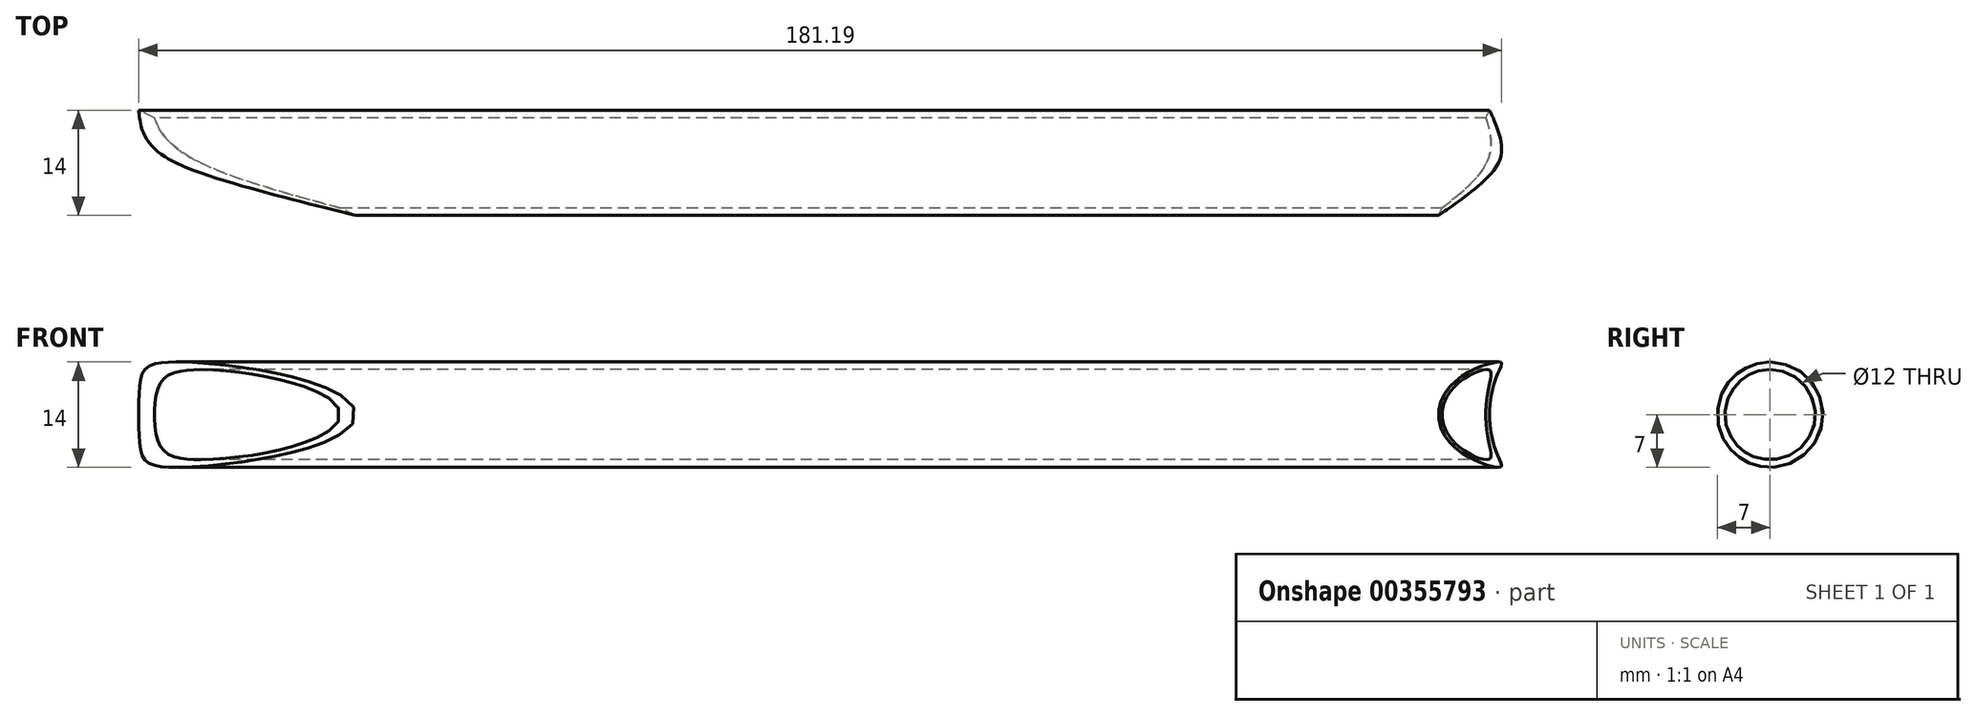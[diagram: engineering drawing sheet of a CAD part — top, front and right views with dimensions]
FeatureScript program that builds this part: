
annotation { "Feature Type Name" : "Feature", "Feature Type Description" : "" }
export const myFeature = defineFeature(function(context is Context, id is Id, definition is map)
    precondition{}
    {
        {
            var Q0;
            Q0=qCreatedBy(makeId("Right.planeOp"),FACE);
            var sketch = newSketch(context, id + "F0", { "sketchPlane" : qUnion([Q0])});
            skCircle(sketch, "E0", {"center": v(0, 0) * mm, "radius": 7 * mm});
            skCircle(sketch, "E1", {"center": v(0, 0) * mm, "radius": 6 * mm});
            skSolve(sketch);
        }
        {
            var Q0;
            Q0=qSketchRegion(id+"F0",true);
            extrude(context, id + "F1", {"entities" : qUnion([Q0]), "depth" : 188.96 * mm});
        }
        {
            var Q0;
            Q0=qCreatedBy(makeId("Right.planeOp"),FACE);
            var sketch = newSketch(context, id + "F2", { "sketchPlane" : qUnion([Q0])});
            skLineSegment(sketch, "E2", {"start": v(0, 75.19) * mm, "end": v(0, -75.52) * mm, "construction": true});
            skSolve(sketch);
        }
        {
            var Q0;
            Q0=sQuery(id+"F2.wireOp",EDGE,"E2");
            var Q1;
            Q1=qBodyType(qCreatedBy(id+"F4",EDGE),BodyType.WIRE);
            cPlane(context, id + "F3", {"entities" : qUnion([Q0, Q1]), "cplaneType" : CPlaneType.LINE_ANGLE, "offset" : 25 * mm, "angle" : 25.89 * degree, "width" : 150 * mm, "height" : 150 * mm});
        }
        {
            var Q0;
            Q0=qCreatedBy(id+"F3.planeOp",FACE);
            var sketch = newSketch(context, id + "F4", { "sketchPlane" : qUnion([Q0])});
            skCircle(sketch, "E3", {"center": v(0, 0) * mm, "radius": 8 * mm});
            skSolve(sketch);
        }
        {
            var Q0;
            Q0=qSketchRegion(id+"F4",true);
            extrude(context, id + "F5", {"entities" : qUnion([Q0]), "operationType" : NewBodyOperationType.REMOVE, "endBound" : BoundingType.SYMMETRIC, "oppositeDirection" : true, "depth" : 70 * mm});
        }
        {
            var Q0;
            Q0=makeQuery(id+"F1.opExtrude","CAP_FACE",FACE,{"disambiguationData":[OSD([sQuery(id+"F0.wireOp",EDGE,"E0"),sQuery(id+"F0.wireOp",EDGE,"E1")])],"isStart":false});
            var sketch = newSketch(context, id + "F6", { "sketchPlane" : qUnion([Q0])});
            skLineSegment(sketch, "E4", {"start": v(0, -7) * mm, "end": v(0, 7) * mm, "construction": true});
            skSolve(sketch);
        }
        {
            var Q0;
            Q0=sQuery(id+"F6.wireOp",EDGE,"E4");
            cPlane(context, id + "F7", {"entities" : qUnion([Q0]), "cplaneType" : CPlaneType.LINE_ANGLE, "offset" : 25 * mm, "angle" : 64.11 * degree, "width" : 150 * mm, "height" : 150 * mm});
        }
        {
            var Q0;
            Q0=qCreatedBy(id+"F7.planeOp",FACE);
            var sketch = newSketch(context, id + "F8", { "sketchPlane" : qUnion([Q0])});
            skCircle(sketch, "E5", {"center": v(-170, 0) * mm, "radius": 8 * mm});
            skLineSegment(sketch, "E6", {"start": v(-174.76, 5.26) * mm, "end": v(-176, 6.09) * mm});
            skEllipse(sketch, "E7.0", {"center": v(-170, 0) * mm, "majorRadius": 7 * mm, "minorRadius": 3.06 * mm, "majorAxis": v(0, 1), "construction": true});
            skLineSegment(sketch, "E8", {"start": v(-170, 7) * mm, "end": v(-170, -7) * mm, "construction": true});
            skLineSegment(sketch, "E9", {"start": v(-170, 0) * mm, "end": v(-174.34, 0) * mm, "construction": true});
            skSolve(sketch);
        }
        {
            var Q0;
            Q0=qSketchRegion(id+"F8",true);
            extrude(context, id + "F9", {"entities" : qUnion([Q0]), "operationType" : NewBodyOperationType.REMOVE, "endBound" : BoundingType.SYMMETRIC, "oppositeDirection" : true, "depth" : 30 * mm});
        }
    });
